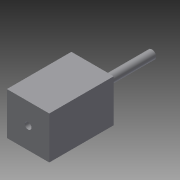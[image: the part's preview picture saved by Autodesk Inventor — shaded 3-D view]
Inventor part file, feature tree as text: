
AUTODESK INVENTOR PART (.ipt)
format: ipt  version: 2013 (Build 170138000, 138)  size: 87,040 bytes
history: native  units: in
note: dims shown in document units (in); Inventor stores cm internally (conversion verified against a paired STEP export)
features: extrude x3, sketch x3
ambient origin geometry x8: Origin, YZ Plane, XZ Plane, XY Plane, X Axis, Y Axis, Z Axis, Center Point
bodies: Solid1 (feature_tree)
feature tree (6):
  extrude  "Extrusion1"  Depth=2.5in
  extrude  "Extrusion2"  Depth=0.5in
  extrude  "Extrusion3"  Depth=1.25in
  sketch  "Sketch1"  dims[d0=2.5in d1=2.5in]
  sketch  "Sketch2"  dims[d2=3.805in d3=0.0in d4=0.5in]
  sketch  "Sketch3"  dims[d5=1.25in d6=1.25in d7=3.5in d8=0.0in d9=2.5in d10=0.3937in d11=3.5in d12=0.0in]
